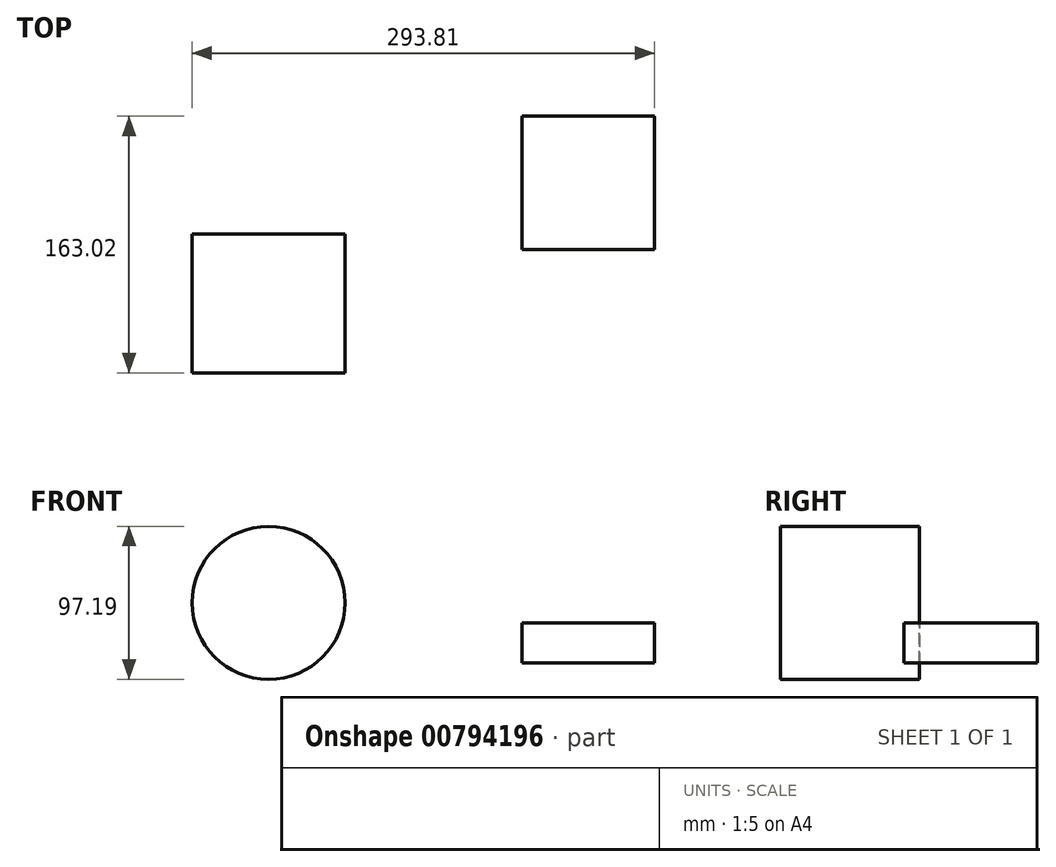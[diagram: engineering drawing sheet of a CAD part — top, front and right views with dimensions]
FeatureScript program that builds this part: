
annotation { "Feature Type Name" : "Feature", "Feature Type Description" : "" }
export const myFeature = defineFeature(function(context is Context, id is Id, definition is map)
    precondition{}
    {
        {
            var Q0;
            Q0=qCreatedBy(makeId("Front.planeOp"),FACE);
            var sketch = newSketch(context, id + "F0", { "sketchPlane" : qUnion([Q0])});
            skCircle(sketch, "E0", {"center": v(-104.96, 38.03) * mm, "radius": 48.6 * mm});
            skSolve(sketch);
        }
        {
            var Q0;
            Q0 = qSketchRegion(id + "F0", true);
            extrude(context, id + "F1", {"entities" : qUnion([Q0]), "depth" : 25.4 * mm, "offsetDistance" : 25.4 * mm});
        }
        {
            var Q0;
            Q0=makeQuery(id+"F1.opExtrude","CAP_FACE",FACE,{"disambiguationData":[OSD([sQuery(id+"F0.wireOp",EDGE,"E0")])],"isStart":false});
            extrude(context, id + "F2", {"entities" : qUnion([Q0]), "operationType" : NewBodyOperationType.ADD, "depth" : 62.74 * mm, "offsetDistance" : 25.4 * mm});
        }
        {
            var Q0;
            Q0=qCreatedBy(makeId("Top.planeOp"),FACE);
            var sketch = newSketch(context, id + "F3", { "sketchPlane" : qUnion([Q0])});
            skLineSegment(sketch, "E1.bottom", {"start": v(55.93, 74.88) * mm, "end": v(140.26, 74.88) * mm});
            skLineSegment(sketch, "E1.top", {"start": v(55.93, -9.86) * mm, "end": v(140.26, -9.86) * mm});
            skLineSegment(sketch, "E1.left", {"start": v(55.93, 74.88) * mm, "end": v(55.93, -9.86) * mm});
            skLineSegment(sketch, "E1.right", {"start": v(140.26, 74.88) * mm, "end": v(140.26, -9.86) * mm});
            skSolve(sketch);
        }
        {
            var Q0;
            Q0 = qSketchRegion(id + "F3", true);
            extrude(context, id + "F4", {"entities" : qUnion([Q0]), "depth" : 25.4 * mm, "offsetDistance" : 25.4 * mm});
        }
    });
